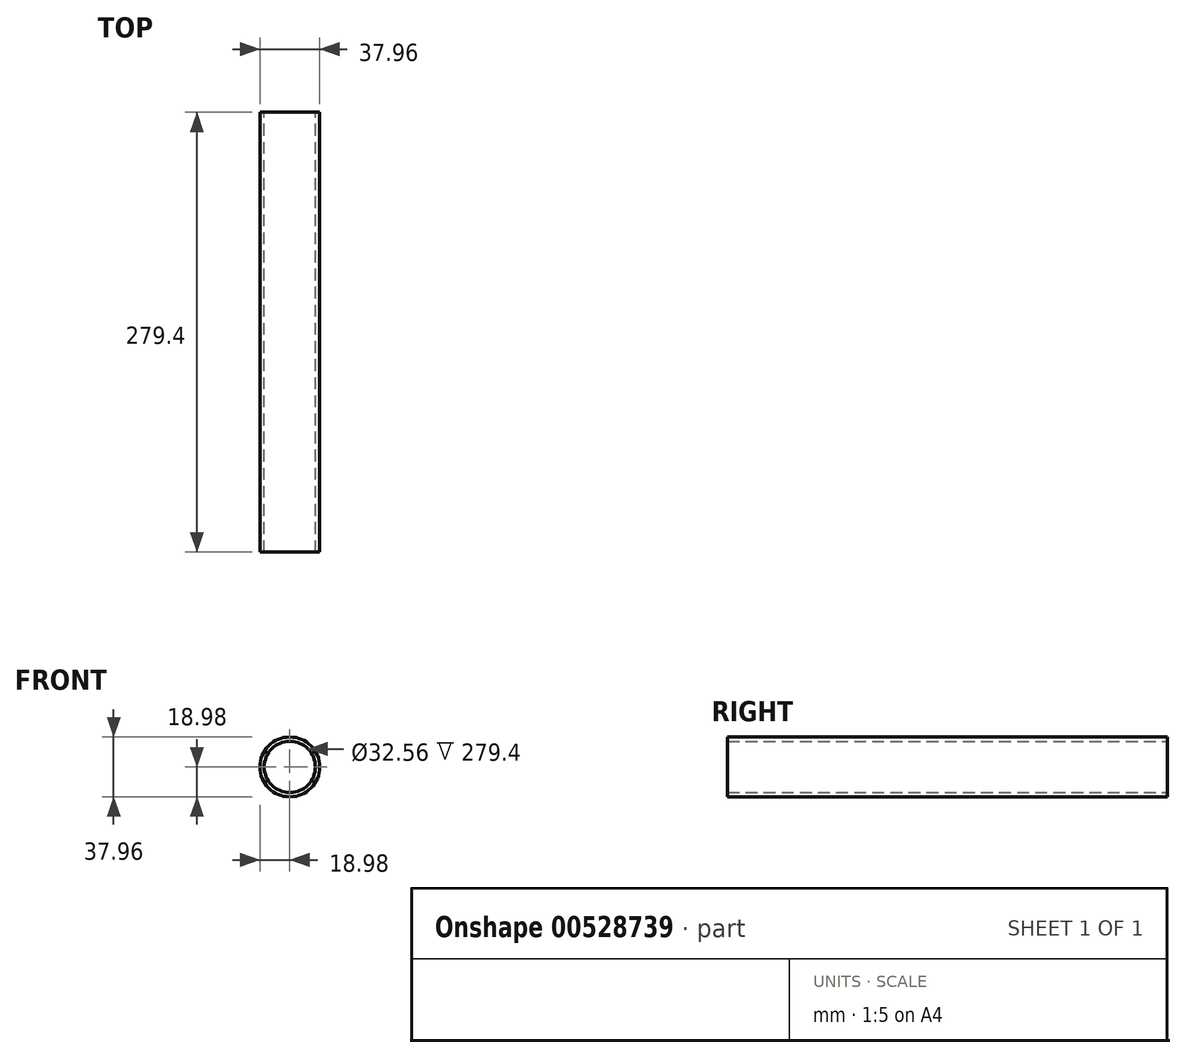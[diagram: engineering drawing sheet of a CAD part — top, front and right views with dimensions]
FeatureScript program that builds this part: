
annotation { "Feature Type Name" : "Feature", "Feature Type Description" : "" }
export const myFeature = defineFeature(function(context is Context, id is Id, definition is map)
    precondition{}
    {
        {
            var Q0;
            Q0=qCreatedBy(makeId("Front.planeOp"),FACE);
            var sketch = newSketch(context, id + "F0", { "sketchPlane" : qUnion([Q0])});
            skCircle(sketch, "E0", {"center": v(0, 0) * mm, "radius": 18.98 * mm});
            skCircle(sketch, "E1", {"center": v(0, 0) * mm, "radius": 16.28 * mm});
            skSolve(sketch);
        }
        {
            var Q0;
            Q0=makeQuery(id+"F0.imprint","IMPRINT",FACE,{"disambiguationData":[TD([[makeQuery(id+"F0.imprint","IMPRINT",EDGE,{"derivedFrom":sQuery(id+"F0.wireOp",EDGE,"E0")}),1.0]])]});
            extrude(context, id + "F1", {"entities" : qUnion([Q0]), "depth" : 279.4 * mm, "offsetDistance" : 25.4 * mm});
        }
    });
